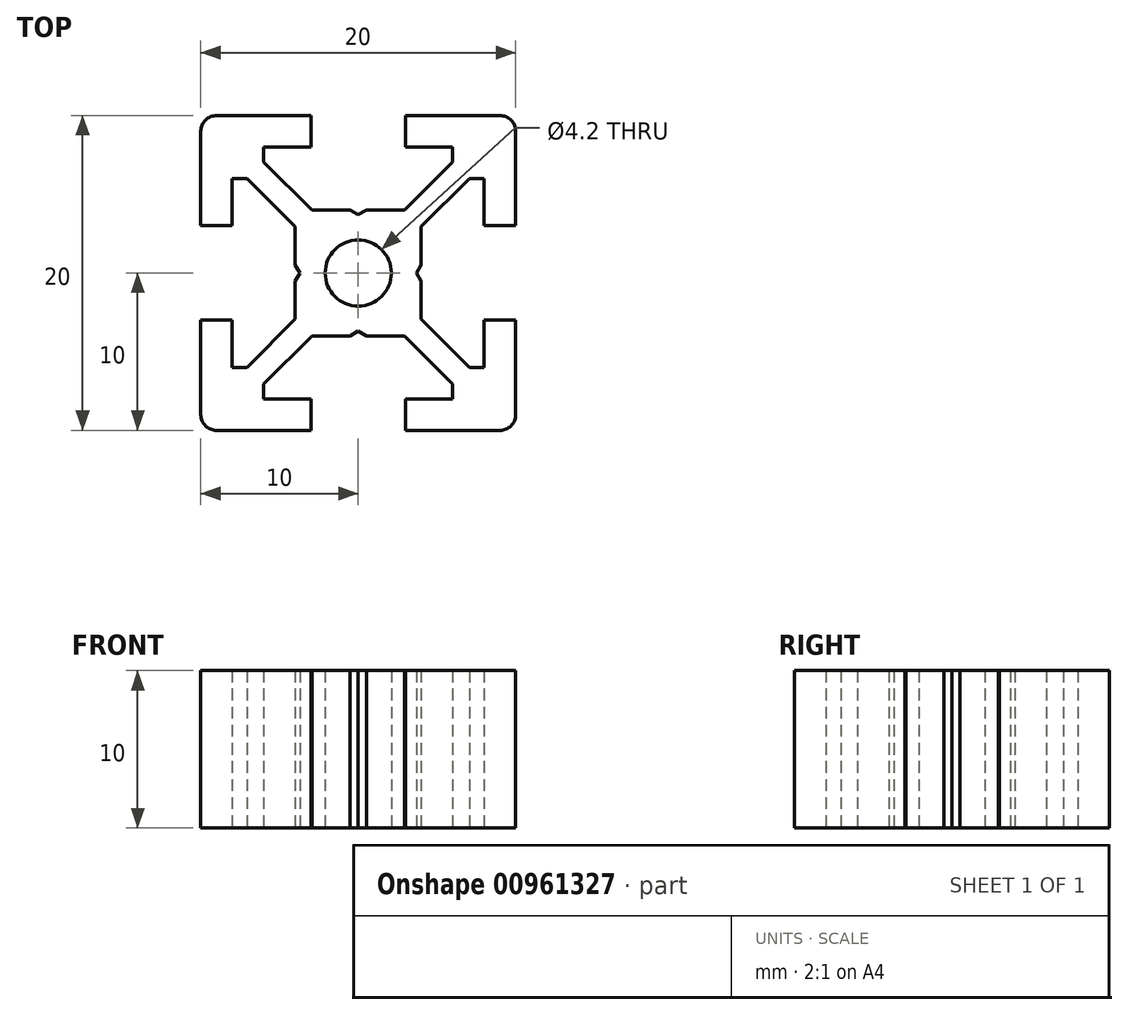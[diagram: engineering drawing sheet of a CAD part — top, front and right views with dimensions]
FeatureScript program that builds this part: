
annotation { "Feature Type Name" : "Feature", "Feature Type Description" : "" }
export const myFeature = defineFeature(function(context is Context, id is Id, definition is map)
    precondition{}
    {
        {
            var Q0;
            Q0=qCreatedBy(makeId("Top.planeOp"),FACE);
            var sketch = newSketch(context, id + "F0", { "sketchPlane" : qUnion([Q0])});
            skLineSegment(sketch, "E0", {"start": v(-8, -3) * mm, "end": v(-10, -3) * mm});
            skLineSegment(sketch, "E1", {"start": v(-10, -3) * mm, "end": v(-10, -9) * mm});
            skArc(sketch, "E2", {"start": v(-10, -9) * mm, "mid": v(-9.7, -9.7) * mm, "end": v(-9, -10) * mm});
            skLineSegment(sketch, "E3", {"start": v(-9, -10) * mm, "end": v(-3, -10) * mm});
            skLineSegment(sketch, "E4", {"start": v(-3, -10) * mm, "end": v(-3, -8) * mm});
            skLineSegment(sketch, "E5", {"start": v(-3, -8) * mm, "end": v(-6, -8) * mm});
            skLineSegment(sketch, "E6", {"start": v(-6, -8) * mm, "end": v(-6, -7.06) * mm});
            skLineSegment(sketch, "E7", {"start": v(-6, -7.06) * mm, "end": v(-2.94, -4) * mm});
            skLineSegment(sketch, "E8", {"start": v(-2.94, -4) * mm, "end": v(-0.52, -4) * mm});
            skLineSegment(sketch, "E9", {"start": v(-0.52, -4) * mm, "end": v(0, -3.7) * mm});
            skLineSegment(sketch, "E10", {"start": v(0, -3.7) * mm, "end": v(0.52, -4) * mm});
            skLineSegment(sketch, "E11", {"start": v(0.52, -4) * mm, "end": v(2.94, -4) * mm});
            skLineSegment(sketch, "E12", {"start": v(2.94, -4) * mm, "end": v(6, -7.06) * mm});
            skLineSegment(sketch, "E13", {"start": v(6, -7.06) * mm, "end": v(6, -8) * mm});
            skLineSegment(sketch, "E14", {"start": v(6, -8) * mm, "end": v(3, -8) * mm});
            skLineSegment(sketch, "E15", {"start": v(3, -8) * mm, "end": v(3, -10) * mm});
            skLineSegment(sketch, "E16", {"start": v(3, -10) * mm, "end": v(9, -10) * mm});
            skArc(sketch, "E17", {"start": v(9, -10) * mm, "mid": v(9.7, -9.7) * mm, "end": v(10, -9) * mm});
            skLineSegment(sketch, "E18", {"start": v(10, -9) * mm, "end": v(10, -3) * mm});
            skLineSegment(sketch, "E19", {"start": v(10, -3) * mm, "end": v(8, -3) * mm});
            skLineSegment(sketch, "E20", {"start": v(8, -3) * mm, "end": v(8, -6) * mm});
            skLineSegment(sketch, "E21", {"start": v(8, -6) * mm, "end": v(7.06, -6) * mm});
            skLineSegment(sketch, "E22", {"start": v(7.06, -6) * mm, "end": v(4, -2.94) * mm});
            skLineSegment(sketch, "E23", {"start": v(4, -2.94) * mm, "end": v(4, -0.52) * mm});
            skLineSegment(sketch, "E24", {"start": v(4, -0.52) * mm, "end": v(3.7, 0) * mm});
            skLineSegment(sketch, "E25", {"start": v(3.7, 0) * mm, "end": v(4, 0.52) * mm});
            skLineSegment(sketch, "E26", {"start": v(4, 0.52) * mm, "end": v(4, 2.94) * mm});
            skLineSegment(sketch, "E27", {"start": v(4, 2.94) * mm, "end": v(7.06, 6) * mm});
            skLineSegment(sketch, "E28", {"start": v(7.06, 6) * mm, "end": v(8, 6) * mm});
            skLineSegment(sketch, "E29", {"start": v(8, 6) * mm, "end": v(8, 3) * mm});
            skLineSegment(sketch, "E30", {"start": v(8, 3) * mm, "end": v(10, 3) * mm});
            skLineSegment(sketch, "E31", {"start": v(10, 3) * mm, "end": v(10, 9) * mm});
            skArc(sketch, "E32", {"start": v(10, 9) * mm, "mid": v(9.7, 9.7) * mm, "end": v(9, 10) * mm});
            skLineSegment(sketch, "E33", {"start": v(9, 10) * mm, "end": v(3, 10) * mm});
            skLineSegment(sketch, "E34", {"start": v(3, 10) * mm, "end": v(3, 8) * mm});
            skLineSegment(sketch, "E35", {"start": v(3, 8) * mm, "end": v(6, 8) * mm});
            skLineSegment(sketch, "E36", {"start": v(6, 8) * mm, "end": v(6, 7.06) * mm});
            skLineSegment(sketch, "E37", {"start": v(6, 7.06) * mm, "end": v(2.94, 4) * mm});
            skLineSegment(sketch, "E38", {"start": v(2.94, 4) * mm, "end": v(0.52, 4) * mm});
            skLineSegment(sketch, "E39", {"start": v(0.52, 4) * mm, "end": v(0, 3.7) * mm});
            skLineSegment(sketch, "E40", {"start": v(0, 3.7) * mm, "end": v(-0.52, 4) * mm});
            skLineSegment(sketch, "E41", {"start": v(-0.52, 4) * mm, "end": v(-2.94, 4) * mm});
            skLineSegment(sketch, "E42", {"start": v(-2.94, 4) * mm, "end": v(-6, 7.06) * mm});
            skLineSegment(sketch, "E43", {"start": v(-6, 7.06) * mm, "end": v(-6, 8) * mm});
            skLineSegment(sketch, "E44", {"start": v(-6, 8) * mm, "end": v(-3, 8) * mm});
            skLineSegment(sketch, "E45", {"start": v(-3, 8) * mm, "end": v(-3, 10) * mm});
            skLineSegment(sketch, "E46", {"start": v(-3, 10) * mm, "end": v(-9, 10) * mm});
            skArc(sketch, "E47", {"start": v(-9, 10) * mm, "mid": v(-9.7, 9.7) * mm, "end": v(-10, 9) * mm});
            skLineSegment(sketch, "E48", {"start": v(-10, 9) * mm, "end": v(-10, 3) * mm});
            skLineSegment(sketch, "E49", {"start": v(-10, 3) * mm, "end": v(-8, 3) * mm});
            skLineSegment(sketch, "E50", {"start": v(-8, 3) * mm, "end": v(-8, 6) * mm});
            skLineSegment(sketch, "E51", {"start": v(-8, 6) * mm, "end": v(-7.06, 6) * mm});
            skLineSegment(sketch, "E52", {"start": v(-7.06, 6) * mm, "end": v(-4, 2.94) * mm});
            skLineSegment(sketch, "E53", {"start": v(-4, 2.94) * mm, "end": v(-4, 0.52) * mm});
            skLineSegment(sketch, "E54", {"start": v(-4, 0.52) * mm, "end": v(-3.7, 0) * mm});
            skLineSegment(sketch, "E55", {"start": v(-3.7, 0) * mm, "end": v(-4, -0.52) * mm});
            skLineSegment(sketch, "E56", {"start": v(-4, -0.52) * mm, "end": v(-4, -2.94) * mm});
            skLineSegment(sketch, "E57", {"start": v(-4, -2.94) * mm, "end": v(-7.06, -6) * mm});
            skLineSegment(sketch, "E58", {"start": v(-7.06, -6) * mm, "end": v(-8, -6) * mm});
            skLineSegment(sketch, "E59", {"start": v(-8, -6) * mm, "end": v(-8, -3) * mm});
            skCircle(sketch, "E60", {"center": v(0, 0) * mm, "radius": 2.1 * mm});
            skSolve(sketch);
        }
        {
            var Q0;
            Q0=qSketchRegion(id+"F0",true);
            extrude(context, id + "F1", {"entities" : qUnion([Q0]), "depth" : 10 * mm, "offsetDistance" : 25 * mm});
        }
    });
